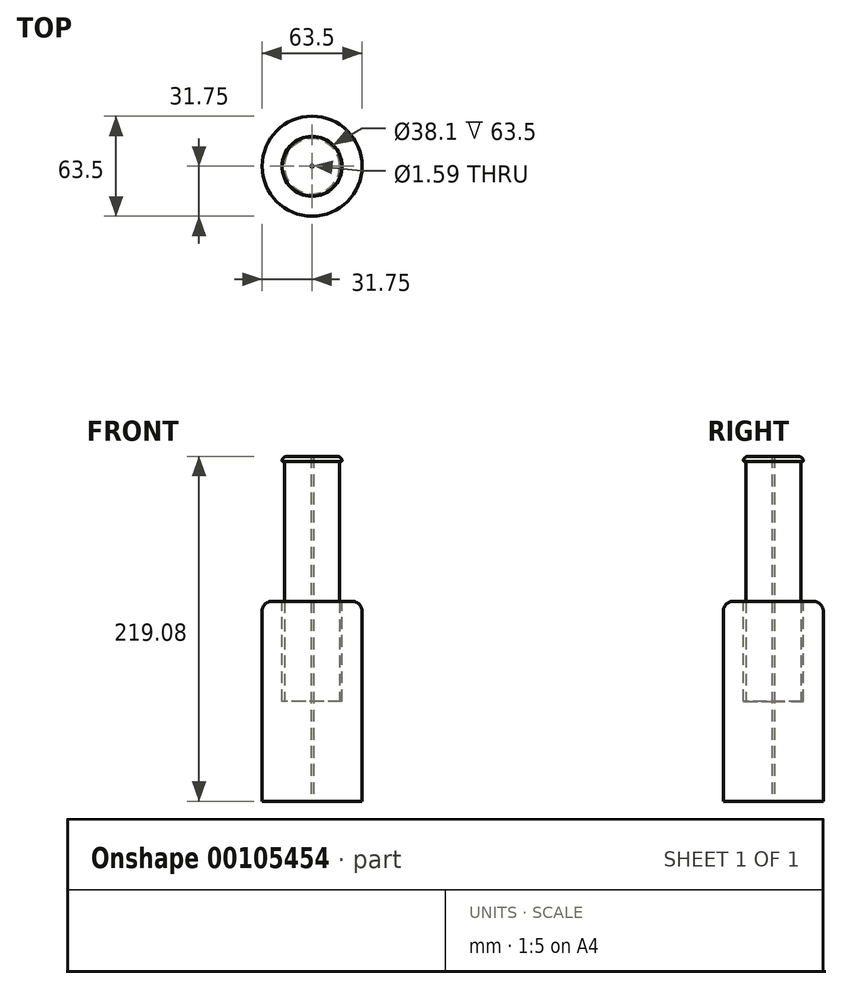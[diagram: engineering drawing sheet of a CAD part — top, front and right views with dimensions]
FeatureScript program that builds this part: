
annotation { "Feature Type Name" : "Feature", "Feature Type Description" : "" }
export const myFeature = defineFeature(function(context is Context, id is Id, definition is map)
    precondition{}
    {
        {
            var Q0;
            Q0=qCreatedBy(makeId("Top.planeOp"),FACE);
            var sketch = newSketch(context, id + "F0", { "sketchPlane" : qUnion([Q0])});
            skCircle(sketch, "E0", {"center": v(0, 0) * mm, "radius": 31.75 * mm});
            skSolve(sketch);
        }
        {
            var Q0;
            Q0 = qSketchRegion(id + "F0", true);
            extrude(context, id + "F1", {"entities" : qUnion([Q0]), "depth" : 127 * mm});
        }
        {
            var Q0;
            Q0=makeQuery(id+"F1.opExtrude","CAP_FACE",FACE,{"disambiguationData":[OSD([sQuery(id+"F0.wireOp",EDGE,"E0")])],"isStart":false});
            var sketch = newSketch(context, id + "F2", { "sketchPlane" : qUnion([Q0])});
            skCircle(sketch, "E1", {"center": v(0, 0) * mm, "radius": 19.05 * mm});
            skSolve(sketch);
        }
        {
            var Q0;
            Q0 = qSketchRegion(id + "F2", true);
            extrude(context, id + "F3", {"entities" : qUnion([Q0]), "operationType" : NewBodyOperationType.REMOVE, "oppositeDirection" : true, "depth" : 63.5 * mm});
        }
        {
            var Q0;
            Q0=makeQuery(id+"F3.boolean.opBoolean","COPY",FACE,{"derivedFrom":makeQuery(id+"F3.opExtrude","CAP_FACE",FACE,{"disambiguationData":[OSD([sQuery(id+"F2.wireOp",EDGE,"E1")])],"isStart":false})});
            var sketch = newSketch(context, id + "F4", { "sketchPlane" : qUnion([Q0])});
            skCircle(sketch, "E2", {"center": v(0, 0) * mm, "radius": 17.53 * mm});
            skSolve(sketch);
        }
        {
            var Q0;
            Q0 = qSketchRegion(id + "F4", true);
            extrude(context, id + "F5", {"entities" : qUnion([Q0]), "operationType" : NewBodyOperationType.ADD, "depth" : 152.4 * mm});
        }
        {
            var Q0;
            Q0=makeQuery(id+"F5.opExtrude","CAP_FACE",FACE,{"disambiguationData":[OSD([sQuery(id+"F4.wireOp",EDGE,"E2")])],"isStart":false});
            var sketch = newSketch(context, id + "F6", { "sketchPlane" : qUnion([Q0])});
            skCircle(sketch, "E3", {"center": v(0, 0) * mm, "radius": 19.05 * mm});
            skSolve(sketch);
        }
        {
            var Q0;
            Q0 = qSketchRegion(id + "F6", true);
            extrude(context, id + "F7", {"entities" : qUnion([Q0]), "operationType" : NewBodyOperationType.ADD, "depth" : 3.17 * mm});
        }
        {
            var Q0;
            Q0=makeQuery(id+"F1.opExtrude","CAP_EDGE",EDGE,{"disambiguationData":[OSD([sQuery(id+"F0.wireOp",EDGE,"E0")])],"isStart":false});
            fillet(context, id + "F8", {"entities" : qUnion([Q0]), "radius" : 6.35 * mm, "tangentPropagation" : true, "allowEdgeOverflow" : false});
        }
        {
            var Q0;
            Q0=makeQuery(id+"F7.opExtrude","CAP_EDGE",EDGE,{"disambiguationData":[OSD([sQuery(id+"F6.wireOp",EDGE,"E3")])],"isStart":false});
            fillet(context, id + "F9", {"entities" : qUnion([Q0]), "radius" : 3.17 * mm, "tangentPropagation" : true, "allowEdgeOverflow" : false});
        }
        {
            var Q0;
            {var subQ0=sQuery(id+"F6.wireOp",EDGE,"E3");Q0=makeQuery(id+"F9.opFillet","BLEND_EDGE",EDGE,{"blendedFrom":[makeQuery(id+"F7.opExtrude","CAP_EDGE",EDGE,{"disambiguationData":[OSD([subQ0])],"isStart":false}),makeQuery(id+"F7.opExtrude","CAP_FACE",FACE,{"disambiguationData":[OSD([subQ0])],"isStart":true})],"blendedInto":[makeQuery(id+"F7.opExtrude","CAP_FACE",FACE,{"disambiguationData":[OSD([subQ0])],"isStart":true})]});}
            fillet(context, id + "F10", {"entities" : qUnion([Q0]), "radius" : 0.5 * mm, "tangentPropagation" : true, "allowEdgeOverflow" : false});
        }
        {
            var Q0;
            Q0=makeQuery(id+"F1.opExtrude","CAP_FACE",FACE,{"disambiguationData":[OSD([sQuery(id+"F0.wireOp",EDGE,"E0")])],"isStart":true});
            var sketch = newSketch(context, id + "F11", { "sketchPlane" : qUnion([Q0])});
            skCircle(sketch, "E4", {"center": v(0, 0) * mm, "radius": 0.8 * mm});
            skSolve(sketch);
        }
        {
            var Q0;
            Q0=sQuery(id+"F11.wireOp",VERTEX,"E4.center");
            var Q1;
            Q1=makeQuery(id+"F1.opExtrude","SWEPT_BODY",BODY,{"disambiguationData":[OSD([sQuery(id+"F0.wireOp",EDGE,"E0")])]});
            hole(context, id + "F12", {"style" : HoleStyle.SIMPLE, "endStyle" : HoleEndStyle.THROUGH, "holeDiameter" : 1.59 * mm, "locations" : qUnion([Q0]), "scope" : qUnion([Q1]), "isTappedThrough" : true});
        }
    });
